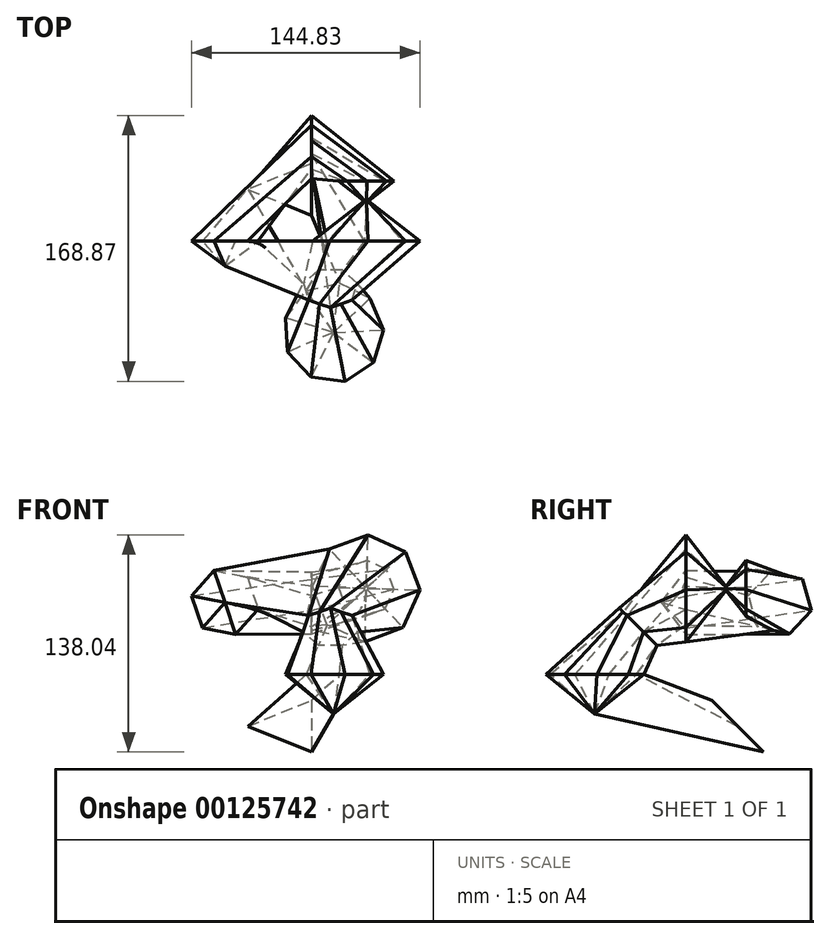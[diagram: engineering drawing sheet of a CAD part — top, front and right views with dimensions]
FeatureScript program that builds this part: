
annotation { "Feature Type Name" : "Feature", "Feature Type Description" : "" }
export const myFeature = defineFeature(function(context is Context, id is Id, definition is map)
    precondition{}
    {
        {
            var Q0;
            Q0=qCreatedBy(makeId("Front.planeOp"),FACE);
            var Q1;
            Q1=qCreatedBy(makeId("Top.planeOp"),FACE);
            cPlane(context, id + "F0", {"entities" : qUnion([Q0, Q1]), "cplaneType" : CPlaneType.MID_PLANE, "offset" : 25.4 * mm, "width" : 152.4 * mm, "height" : 152.4 * mm});
        }
        {
            var Q0;
            Q0=qCreatedBy(makeId("Front.planeOp"),FACE);
            var sketch = newSketch(context, id + "F1", { "sketchPlane" : qUnion([Q0])});
            skCircle(sketch, "E0.cCircle", {"center": v(34.9, 54.67) * mm, "radius": 31.46 * mm, "construction": true});
            skLineSegment(sketch, "E0.0", {"start": v(33.73, 20.64) * mm, "end": v(10, 31.43) * mm});
            skLineSegment(sketch, "E0.1", {"start": v(10, 31.43) * mm, "end": v(0.86, 55.83) * mm});
            skLineSegment(sketch, "E0.2", {"start": v(0.86, 55.83) * mm, "end": v(11.65, 79.56) * mm});
            skLineSegment(sketch, "E0.3", {"start": v(11.65, 79.56) * mm, "end": v(36.06, 88.7) * mm});
            skLineSegment(sketch, "E0.4", {"start": v(36.06, 88.7) * mm, "end": v(59.78, 77.92) * mm});
            skLineSegment(sketch, "E0.5", {"start": v(59.78, 77.92) * mm, "end": v(68.93, 53.51) * mm});
            skLineSegment(sketch, "E0.6", {"start": v(68.93, 53.51) * mm, "end": v(58.14, 29.78) * mm});
            skLineSegment(sketch, "E0.7", {"start": v(58.14, 29.78) * mm, "end": v(33.73, 20.64) * mm});
            skPoint(sketch, "E0.0.midPoint", {"position": v(21.87, 26.03) * mm});
            skSolve(sketch);
        }
        {
            var Q0;
            Q0=qCreatedBy(id+"F0.planeOp",FACE);
            var sketch = newSketch(context, id + "F2", { "sketchPlane" : qUnion([Q0])});
            skCircle(sketch, "E1.cCircle", {"center": v(12.14, 41.93) * mm, "radius": 15.9 * mm, "construction": true});
            skLineSegment(sketch, "E1.0", {"start": v(19.79, 26.04) * mm, "end": v(4.48, 26.04) * mm});
            skLineSegment(sketch, "E1.1", {"start": v(4.48, 26.04) * mm, "end": v(-5.06, 38) * mm});
            skLineSegment(sketch, "E1.2", {"start": v(-5.06, 38) * mm, "end": v(-1.65, 52.93) * mm});
            skLineSegment(sketch, "E1.3", {"start": v(-1.65, 52.93) * mm, "end": v(12.14, 59.57) * mm});
            skLineSegment(sketch, "E1.4", {"start": v(12.14, 59.57) * mm, "end": v(25.93, 52.93) * mm});
            skLineSegment(sketch, "E1.5", {"start": v(25.93, 52.93) * mm, "end": v(29.33, 38) * mm});
            skLineSegment(sketch, "E1.6", {"start": v(29.33, 38) * mm, "end": v(19.79, 26.04) * mm});
            skPoint(sketch, "E1.0.midPoint", {"position": v(12.14, 26.04) * mm});
            skSolve(sketch);
        }
        {
            var Q0;
            Q0=makeQuery(id+"F1.imprint","IMPRINT",FACE,{"disambiguationData":[TD([[makeQuery(id+"F1.imprint","IMPRINT",EDGE,{"derivedFrom":sQuery(id+"F1.wireOp",EDGE,"E0.0")}),-1.0]])]});
            var Q1;
            Q1=makeQuery(id+"F2.imprint","IMPRINT",FACE,{"disambiguationData":[TD([[makeQuery(id+"F2.imprint","IMPRINT",EDGE,{"derivedFrom":sQuery(id+"F2.wireOp",EDGE,"E1.0")}),-1.0]])]});
            loft(context, id + "F3", {"sheetProfilesArray" : [{ "sheetProfileEntities" : qUnion([Q0]) }, { "sheetProfileEntities" : qUnion([Q1]) }]});
        }
        {
            var Q0;
            Q0=qCreatedBy(makeId("Top.planeOp"),FACE);
            var sketch = newSketch(context, id + "F4", { "sketchPlane" : qUnion([Q0])});
            skCircle(sketch, "E2.cCircle", {"center": v(14.13, -57.97) * mm, "radius": 29.86 * mm, "construction": true});
            skLineSegment(sketch, "E2.0", {"start": v(37.37, -36.3) * mm, "end": v(45.87, -56.3) * mm});
            skLineSegment(sketch, "E2.1", {"start": v(45.87, -56.3) * mm, "end": v(39.5, -77.1) * mm});
            skLineSegment(sketch, "E2.2", {"start": v(39.5, -77.1) * mm, "end": v(21.28, -88.93) * mm});
            skLineSegment(sketch, "E2.3", {"start": v(21.28, -88.93) * mm, "end": v(-0.3, -86.28) * mm});
            skLineSegment(sketch, "E2.4", {"start": v(-0.3, -86.28) * mm, "end": v(-15.11, -70.38) * mm});
            skLineSegment(sketch, "E2.5", {"start": v(-15.11, -70.38) * mm, "end": v(-16.25, -48.68) * mm});
            skLineSegment(sketch, "E2.6", {"start": v(-16.25, -48.68) * mm, "end": v(-3.17, -31.32) * mm});
            skLineSegment(sketch, "E2.7", {"start": v(-3.17, -31.32) * mm, "end": v(18, -26.43) * mm});
            skLineSegment(sketch, "E2.8", {"start": v(18, -26.43) * mm, "end": v(37.37, -36.3) * mm});
            skPoint(sketch, "E2.0.midPoint", {"position": v(41.62, -46.3) * mm});
            skSolve(sketch);
        }
        {
            var Q1;
            Q1=makeQuery(id+"F4.imprint","IMPRINT",FACE,{"disambiguationData":[TD([[makeQuery(id+"F4.imprint","IMPRINT",EDGE,{"derivedFrom":sQuery(id+"F4.wireOp",EDGE,"E2.0")}),-1.0]])]});
            var Q2;
            Q2=makeQuery(id+"F3.opLoft","CAP_FACE",FACE,{"disambiguationData":[OSD([makeQuery(id+"F2.imprint","IMPRINT",FACE,{"disambiguationData":[TD([[makeQuery(id+"F2.imprint","IMPRINT",EDGE,{"derivedFrom":sQuery(id+"F2.wireOp",EDGE,"E1.0")}),-1.0]])]})])],"isStart":true});
            loft(context, id + "F5", {"operationType" : NewBodyOperationType.ADD, "sheetProfilesArray" : [{ "sheetProfileEntities" : qUnion([Q1]) }, { "sheetProfileEntities" : qUnion([Q2]) }]});
        }
        {
            var Q0;
            Q0=makeQuery(id+"F3.opLoft","CAP_FACE",FACE,{"disambiguationData":[OSD([makeQuery(id+"F1.imprint","IMPRINT",FACE,{"disambiguationData":[TD([[makeQuery(id+"F1.imprint","IMPRINT",EDGE,{"derivedFrom":sQuery(id+"F1.wireOp",EDGE,"E0.0")}),-1.0]])]})])],"isStart":true});
            extrude(context, id + "F6", {"entities" : qUnion([Q0]), "operationType" : NewBodyOperationType.ADD, "depth" : 25.4 * mm, "hasDraft" : true, "draftAngle" : 50 * degree, "draftPullDirection" : true});
        }
        {
            var Q0;
            Q0=makeQuery(id+"F5.opLoft","CAP_FACE",FACE,{"disambiguationData":[OSD([makeQuery(id+"F4.imprint","IMPRINT",FACE,{"disambiguationData":[TD([[makeQuery(id+"F4.imprint","IMPRINT",EDGE,{"derivedFrom":sQuery(id+"F4.wireOp",EDGE,"E2.0")}),-1.0]])]})])],"isStart":true});
            extrude(context, id + "F7", {"entities" : qUnion([Q0]), "operationType" : NewBodyOperationType.ADD, "depth" : 25.4 * mm, "hasDraft" : true, "draftAngle" : 50 * degree, "draftPullDirection" : true});
        }
        {
            var Q0;
            Q0=makeQuery(id+"F6.opExtrude","CAP_FACE",FACE,{"disambiguationData":[OSD([makeQuery(id+"F1.imprint","IMPRINT",FACE,{"disambiguationData":[TD([[makeQuery(id+"F1.imprint","IMPRINT",EDGE,{"derivedFrom":sQuery(id+"F1.wireOp",EDGE,"E0.0")}),-1.0]])]})])],"isStart":false});
            extrude(context, id + "F8", {"entities" : qUnion([Q0]), "operationType" : NewBodyOperationType.ADD, "depth" : 12.7 * mm, "hasDraft" : true, "draftAngle" : 50 * degree});
        }
        {
            var Q0;
            Q0=qCreatedBy(makeId("Right.planeOp"),FACE);
            var sketch = newSketch(context, id + "F9", { "sketchPlane" : qUnion([Q0])});
            skCircle(sketch, "E3.cCircle", {"center": v(59.87, 45.47) * mm, "radius": 17.84 * mm, "construction": true});
            skLineSegment(sketch, "E3.0", {"start": v(39.8, 50.14) * mm, "end": v(53.88, 65.18) * mm});
            skLineSegment(sketch, "E3.1", {"start": v(53.88, 65.18) * mm, "end": v(73.95, 60.5) * mm});
            skLineSegment(sketch, "E3.2", {"start": v(73.95, 60.5) * mm, "end": v(79.94, 40.8) * mm});
            skLineSegment(sketch, "E3.3", {"start": v(79.94, 40.8) * mm, "end": v(65.86, 25.76) * mm});
            skLineSegment(sketch, "E3.4", {"start": v(65.86, 25.76) * mm, "end": v(45.8, 30.43) * mm});
            skLineSegment(sketch, "E3.5", {"start": v(45.8, 30.43) * mm, "end": v(39.8, 50.14) * mm});
            skPoint(sketch, "E3.0.midPoint", {"position": v(46.85, 57.66) * mm});
            skSolve(sketch);
        }
        {
            var Q1;
            Q1=makeQuery(id+"F9.imprint","IMPRINT",FACE,{"disambiguationData":[TD([[makeQuery(id+"F9.imprint","IMPRINT",EDGE,{"derivedFrom":sQuery(id+"F9.wireOp",EDGE,"E3.0")}),-1.0]])]});
            var Q2;
            Q2=makeQuery(id+"F8.opExtrude","CAP_FACE",FACE,{"disambiguationData":[OSD([makeQuery(id+"F1.imprint","IMPRINT",FACE,{"disambiguationData":[TD([[makeQuery(id+"F1.imprint","IMPRINT",EDGE,{"derivedFrom":sQuery(id+"F1.wireOp",EDGE,"E0.0")}),-1.0]])]})])],"isStart":false});
            loft(context, id + "F10", {"operationType" : NewBodyOperationType.ADD, "sheetProfilesArray" : [{ "sheetProfileEntities" : qUnion([Q1]) }, { "sheetProfileEntities" : qUnion([Q2]) }]});
        }
        {
            var Q0;
            Q0=qCreatedBy(makeId("Front.planeOp"),FACE);
            var sketch = newSketch(context, id + "F11", { "sketchPlane" : qUnion([Q0])});
            skCircle(sketch, "E4.cCircle", {"center": v(-54.84, 45.68) * mm, "radius": 18.61 * mm, "construction": true});
            skLineSegment(sketch, "E4.0", {"start": v(-40.62, 61.8) * mm, "end": v(-33.77, 41.42) * mm});
            skLineSegment(sketch, "E4.1", {"start": v(-33.77, 41.42) * mm, "end": v(-47.99, 25.3) * mm});
            skLineSegment(sketch, "E4.2", {"start": v(-47.99, 25.3) * mm, "end": v(-69.05, 29.57) * mm});
            skLineSegment(sketch, "E4.3", {"start": v(-69.05, 29.57) * mm, "end": v(-75.9, 49.94) * mm});
            skLineSegment(sketch, "E4.4", {"start": v(-75.9, 49.94) * mm, "end": v(-61.68, 66.05) * mm});
            skLineSegment(sketch, "E4.5", {"start": v(-61.68, 66.05) * mm, "end": v(-40.62, 61.8) * mm});
            skPoint(sketch, "E4.0.midPoint", {"position": v(-37.2, 51.6) * mm});
            skSolve(sketch);
        }
        {
            var Q1;
            Q1=makeQuery(id+"F11.imprint","IMPRINT",FACE,{"disambiguationData":[TD([[makeQuery(id+"F11.imprint","IMPRINT",EDGE,{"derivedFrom":sQuery(id+"F11.wireOp",EDGE,"E4.0")}),-1.0]])]});
            var Q2;
            Q2=makeQuery(id+"F10.opLoft","CAP_FACE",FACE,{"disambiguationData":[OSD([makeQuery(id+"F9.imprint","IMPRINT",FACE,{"disambiguationData":[TD([[makeQuery(id+"F9.imprint","IMPRINT",EDGE,{"derivedFrom":sQuery(id+"F9.wireOp",EDGE,"E3.0")}),-1.0]])]})])],"isStart":true});
            loft(context, id + "F12", {"operationType" : NewBodyOperationType.ADD, "sheetProfilesArray" : [{ "sheetProfileEntities" : qUnion([Q1]) }, { "sheetProfileEntities" : qUnion([Q2]) }]});
        }
        {
            var Q0;
            Q0=makeQuery(id+"F12.opLoft","CAP_FACE",FACE,{"disambiguationData":[OSD([makeQuery(id+"F11.imprint","IMPRINT",FACE,{"disambiguationData":[TD([[makeQuery(id+"F11.imprint","IMPRINT",EDGE,{"derivedFrom":sQuery(id+"F11.wireOp",EDGE,"E4.0")}),-1.0]])]})])],"isStart":true});
            extrude(context, id + "F13", {"entities" : qUnion([Q0]), "operationType" : NewBodyOperationType.ADD, "depth" : 25.4 * mm, "hasDraft" : true, "draftAngle" : 50 * degree, "draftPullDirection" : true});
        }
        {
            var Q1;
            Q1=makeQuery(id+"F3.opLoft","SWEPT_FACE",FACE,{"disambiguationData":[OSD([sQuery(id+"F1.wireOp",EDGE,"E0.1"),sQuery(id+"F1.wireOp",EDGE,"E0.2"),sQuery(id+"F1.wireOp",EDGE,"E0.3"),sQuery(id+"F2.wireOp",EDGE,"E1.1"),sQuery(id+"F2.wireOp",EDGE,"E1.2"),sQuery(id+"F2.wireOp",EDGE,"E1.3")])]});
            var Q2;
            Q2=makeQuery(id+"F13.opExtrude","SWEPT_FACE",FACE,{"disambiguationData":[OSD([sQuery(id+"F9.wireOp",EDGE,"E3.0"),sQuery(id+"F9.wireOp",EDGE,"E3.5"),sQuery(id+"F11.wireOp",EDGE,"E4.0"),sQuery(id+"F11.wireOp",EDGE,"E4.5")])]});
            loft(context, id + "F14", {"operationType" : NewBodyOperationType.ADD, "sheetProfilesArray" : [{ "sheetProfileEntities" : qUnion([Q1]) }, { "sheetProfileEntities" : qUnion([Q2]) }]});
        }
        {
            var Q1;
            Q1=makeQuery(id+"F6.opExtrude","SWEPT_FACE",FACE,{"disambiguationData":[OSD([sQuery(id+"F1.wireOp",EDGE,"E0.0"),sQuery(id+"F1.wireOp",EDGE,"E0.1"),sQuery(id+"F1.wireOp",EDGE,"E0.7")])]});
            var Q2;
            Q2=makeQuery(id+"F10.opLoft","SWEPT_FACE",FACE,{"disambiguationData":[OSD([sQuery(id+"F1.wireOp",EDGE,"E0.0"),sQuery(id+"F1.wireOp",EDGE,"E0.1"),sQuery(id+"F1.wireOp",EDGE,"E0.2"),sQuery(id+"F1.wireOp",EDGE,"E0.7"),sQuery(id+"F9.wireOp",EDGE,"E3.5")])]});
            loft(context, id + "F15", {"operationType" : NewBodyOperationType.ADD, "sheetProfilesArray" : [{ "sheetProfileEntities" : qUnion([Q1]) }, { "sheetProfileEntities" : qUnion([Q2]) }]});
        }
        {
            var Q0;
            Q0=qCreatedBy(id+"F0.planeOp",FACE);
            var sketch = newSketch(context, id + "F16", { "sketchPlane" : qUnion([Q0])});
            skCircle(sketch, "E5.cCircle", {"center": v(-13.4, -46.54) * mm, "radius": 13.4 * mm, "construction": true});
            skLineSegment(sketch, "E5.0", {"start": v(0, -23.32) * mm, "end": v(0, -69.76) * mm});
            skLineSegment(sketch, "E5.1", {"start": v(0, -69.76) * mm, "end": v(-40.22, -46.54) * mm});
            skLineSegment(sketch, "E5.2", {"start": v(-40.22, -46.54) * mm, "end": v(0, -23.32) * mm});
            skPoint(sketch, "E5.0.midPoint", {"position": v(0, -46.54) * mm});
            skSolve(sketch);
        }
        {
            var Q1;
            Q1=makeQuery(id+"F16.imprint","IMPRINT",FACE,{"disambiguationData":[TD([[makeQuery(id+"F16.imprint","IMPRINT",EDGE,{"derivedFrom":sQuery(id+"F16.wireOp",EDGE,"E5.0")}),-1.0]])]});
            var Q2;
            Q2=makeQuery(id+"F7.opExtrude","SWEPT_FACE",FACE,{"disambiguationData":[OSD([sQuery(id+"F4.wireOp",EDGE,"E2.6"),sQuery(id+"F4.wireOp",EDGE,"E2.7"),sQuery(id+"F4.wireOp",EDGE,"E2.8")])]});
            loft(context, id + "F17", {"operationType" : NewBodyOperationType.ADD, "sheetProfilesArray" : [{ "sheetProfileEntities" : qUnion([Q1]) }, { "sheetProfileEntities" : qUnion([Q2]) }]});
        }
    });
